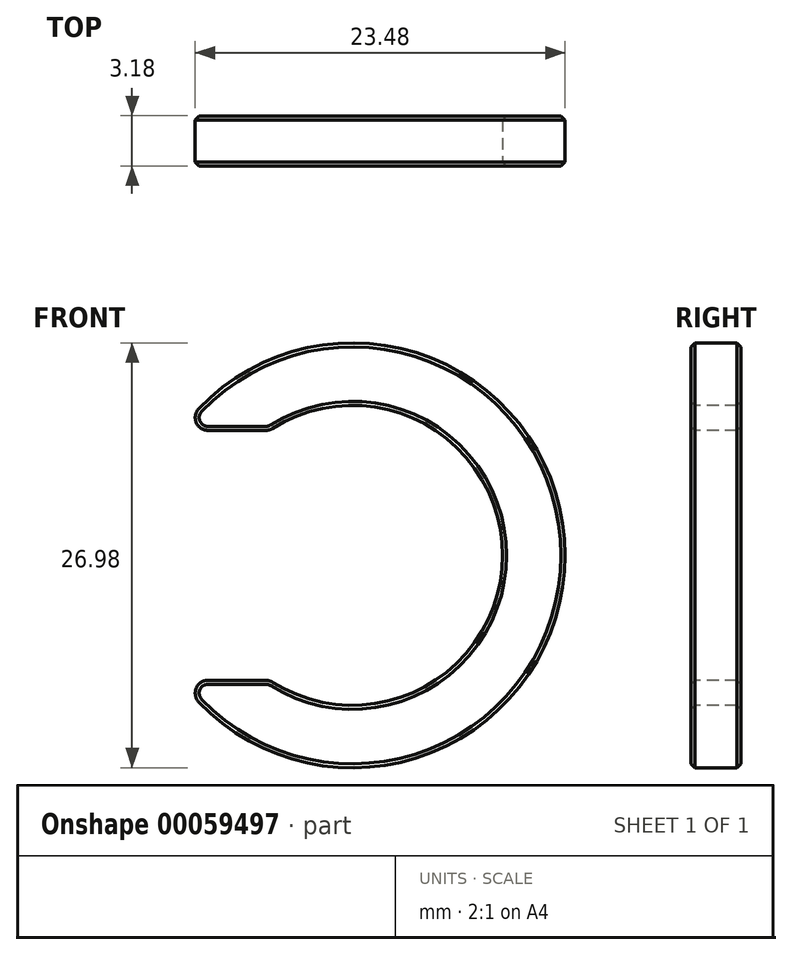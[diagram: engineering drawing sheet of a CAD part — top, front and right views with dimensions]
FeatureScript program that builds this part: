
annotation { "Feature Type Name" : "Feature", "Feature Type Description" : "" }
export const myFeature = defineFeature(function(context is Context, id is Id, definition is map)
    precondition{}
    {
        {
            var Q0;
            Q0=qCreatedBy(makeId("Front.planeOp"),FACE);
            var sketch = newSketch(context, id + "F0", { "sketchPlane" : qUnion([Q0])});
            skArc(sketch, "E0", {"start": v(-9.77, -9.31) * mm, "mid": v(13.5, 0) * mm, "end": v(-9.77, 9.31) * mm});
            skCircle(sketch, "E1", {"center": v(0, 0) * mm, "radius": 11.11 * mm, "construction": true});
            skPoint(sketch, "E2", {"position": v(0, 13.5) * mm});
            skPoint(sketch, "E3", {"position": v(0, 11.11) * mm});
            skArc(sketch, "E4", {"start": v(-5.07, -8.06) * mm, "mid": v(9.53, 0) * mm, "end": v(-5.07, 8.06) * mm});
            skPoint(sketch, "E5", {"position": v(0, 9.53) * mm});
            skLineSegment(sketch, "E6", {"start": v(-9.18, 7.94) * mm, "end": v(-5.5, 7.94) * mm});
            skLineSegment(sketch, "E7", {"start": v(-9.18, -7.94) * mm, "end": v(-5.5, -7.94) * mm});
            skPoint(sketch, "E8.visualSharp", {"position": v(-10.91, 7.94) * mm});
            skArc(sketch, "E8.filletArc", {"start": v(-9.77, 9.31) * mm, "mid": v(-9.93, 8.43) * mm, "end": v(-9.18, 7.94) * mm});
            skPoint(sketch, "E9.visualSharp", {"position": v(-5.27, 7.94) * mm});
            skArc(sketch, "E9.filletArc", {"start": v(-5.5, 7.94) * mm, "mid": v(-5.28, 7.97) * mm, "end": v(-5.07, 8.06) * mm});
            skPoint(sketch, "E10.visualSharp", {"position": v(-10.91, -7.94) * mm});
            skArc(sketch, "E10.filletArc", {"start": v(-9.18, -7.94) * mm, "mid": v(-9.93, -8.43) * mm, "end": v(-9.77, -9.31) * mm});
            skPoint(sketch, "E11.visualSharp", {"position": v(-5.27, -7.94) * mm});
            skArc(sketch, "E11.filletArc", {"start": v(-5.07, -8.06) * mm, "mid": v(-5.28, -7.97) * mm, "end": v(-5.5, -7.94) * mm});
            skSolve(sketch);
        }
        {
            var Q0;
            Q0 = qSketchRegion(id + "F0", true);
            extrude(context, id + "F1", {"entities" : qUnion([Q0]), "oppositeDirection" : true, "depth" : 3.17 * mm});
        }
        {
            var Q0;
            Q0=makeQuery(id+"F1.opExtrude","CAP_EDGE",EDGE,{"disambiguationData":[OSD([sQuery(id+"F0.wireOp",EDGE,"E0")])],"isStart":true});
            var Q1;
            Q1=makeQuery(id+"F1.opExtrude","CAP_EDGE",EDGE,{"disambiguationData":[OSD([sQuery(id+"F0.wireOp",EDGE,"E0")])],"isStart":false});
            chamfer(context, id + "F2", {"entities" : qUnion([Q0, Q1]), "width" : 0.25 * mm, "tangentPropagation" : true});
        }
    });
